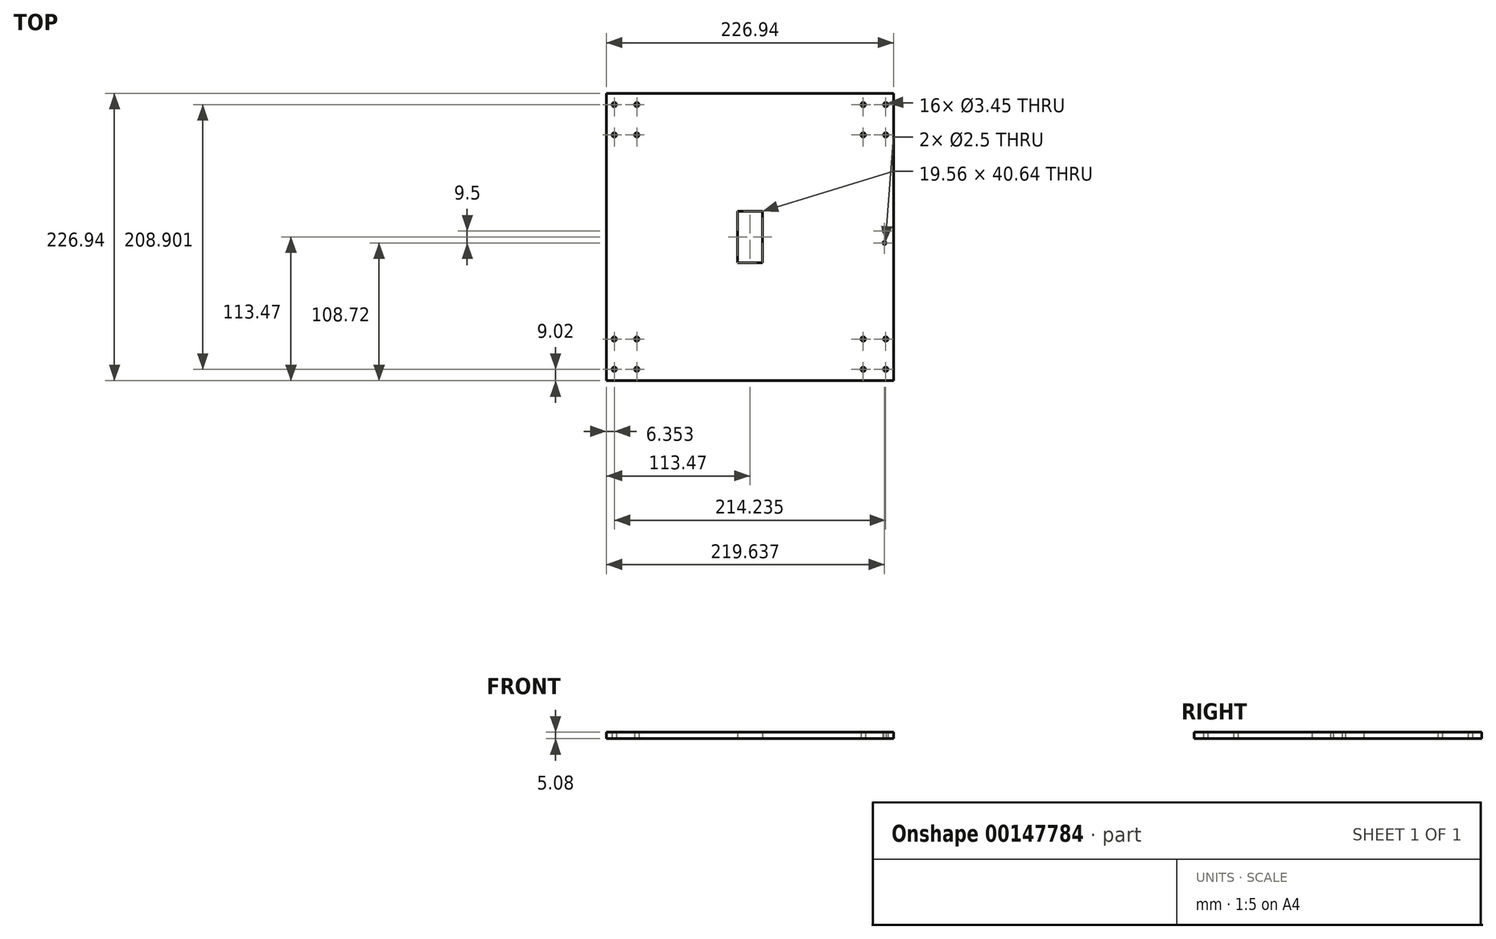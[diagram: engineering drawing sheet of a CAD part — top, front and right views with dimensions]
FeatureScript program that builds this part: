
annotation { "Feature Type Name" : "Feature", "Feature Type Description" : "" }
export const myFeature = defineFeature(function(context is Context, id is Id, definition is map)
    precondition{}
    {
        {
            var Q0;
            Q0=qCreatedBy(makeId("Top.planeOp"),FACE);
            var sketch = newSketch(context, id + "F0", { "sketchPlane" : qUnion([Q0])});
            skLineSegment(sketch, "E0.bottom", {"start": v(113.47, -113.47) * mm, "end": v(-113.47, -113.47) * mm});
            skLineSegment(sketch, "E0.top", {"start": v(113.47, 113.47) * mm, "end": v(-113.47, 113.47) * mm});
            skLineSegment(sketch, "E0.left", {"start": v(113.47, -113.47) * mm, "end": v(113.47, 113.47) * mm});
            skLineSegment(sketch, "E0.right", {"start": v(-113.47, -113.47) * mm, "end": v(-113.47, 113.47) * mm});
            skPoint(sketch, "E0.middle", {"position": v(0, 0) * mm});
            skLineSegment(sketch, "E1", {"start": v(-107.12, 113.47) * mm, "end": v(-107.12, 104.45) * mm, "construction": true});
            skLineSegment(sketch, "E2", {"start": v(-107.12, 104.45) * mm, "end": v(-113.47, 104.45) * mm, "construction": true});
            skLineSegment(sketch, "E3.bottom", {"start": v(-98.23, 92.51) * mm, "end": v(98.23, 92.51) * mm, "construction": true});
            skLineSegment(sketch, "E3.top", {"start": v(-98.23, -92.51) * mm, "end": v(98.23, -92.51) * mm, "construction": true});
            skLineSegment(sketch, "E3.left", {"start": v(-98.23, 92.51) * mm, "end": v(-98.23, -92.51) * mm, "construction": true});
            skLineSegment(sketch, "E3.right", {"start": v(98.23, 92.51) * mm, "end": v(98.23, -92.51) * mm, "construction": true});
            skLineSegment(sketch, "E4.bottom", {"start": v(-107.12, 104.45) * mm, "end": v(-89.34, 104.45) * mm, "construction": true});
            skLineSegment(sketch, "E4.top", {"start": v(-107.12, 80.57) * mm, "end": v(-89.34, 80.57) * mm, "construction": true});
            skLineSegment(sketch, "E4.left", {"start": v(-107.12, 104.45) * mm, "end": v(-107.12, 80.57) * mm, "construction": true});
            skLineSegment(sketch, "E4.right", {"start": v(-89.34, 104.45) * mm, "end": v(-89.34, 80.57) * mm, "construction": true});
            skPoint(sketch, "E4.middle", {"position": v(-98.23, 92.51) * mm});
            skLineSegment(sketch, "E5.bottom", {"start": v(107.12, 104.45) * mm, "end": v(89.34, 104.45) * mm, "construction": true});
            skLineSegment(sketch, "E5.top", {"start": v(107.12, 80.57) * mm, "end": v(89.34, 80.57) * mm, "construction": true});
            skLineSegment(sketch, "E5.left", {"start": v(107.12, 104.45) * mm, "end": v(107.12, 80.57) * mm, "construction": true});
            skLineSegment(sketch, "E5.right", {"start": v(89.34, 104.45) * mm, "end": v(89.34, 80.57) * mm, "construction": true});
            skPoint(sketch, "E5.middle", {"position": v(98.23, 92.51) * mm});
            skLineSegment(sketch, "E6.bottom", {"start": v(107.12, -104.45) * mm, "end": v(89.34, -104.45) * mm, "construction": true});
            skLineSegment(sketch, "E6.top", {"start": v(107.12, -80.57) * mm, "end": v(89.34, -80.57) * mm, "construction": true});
            skLineSegment(sketch, "E6.left", {"start": v(107.12, -104.45) * mm, "end": v(107.12, -80.57) * mm, "construction": true});
            skLineSegment(sketch, "E6.right", {"start": v(89.34, -104.45) * mm, "end": v(89.34, -80.57) * mm, "construction": true});
            skPoint(sketch, "E6.middle", {"position": v(98.23, -92.51) * mm});
            skLineSegment(sketch, "E7.bottom", {"start": v(-89.34, -104.45) * mm, "end": v(-107.12, -104.45) * mm, "construction": true});
            skLineSegment(sketch, "E7.top", {"start": v(-89.34, -80.57) * mm, "end": v(-107.12, -80.57) * mm, "construction": true});
            skLineSegment(sketch, "E7.left", {"start": v(-89.34, -104.45) * mm, "end": v(-89.34, -80.57) * mm, "construction": true});
            skLineSegment(sketch, "E7.right", {"start": v(-107.12, -104.45) * mm, "end": v(-107.12, -80.57) * mm, "construction": true});
            skPoint(sketch, "E7.middle", {"position": v(-98.23, -92.51) * mm});
            skCircle(sketch, "E8", {"center": v(-107.12, 104.45) * mm, "radius": 1.73 * mm});
            skCircle(sketch, "E9", {"center": v(-89.34, 104.45) * mm, "radius": 1.73 * mm});
            skCircle(sketch, "E10", {"center": v(-89.34, 80.57) * mm, "radius": 1.73 * mm});
            skCircle(sketch, "E11", {"center": v(-107.12, 80.57) * mm, "radius": 1.73 * mm});
            skCircle(sketch, "E12", {"center": v(107.12, 80.57) * mm, "radius": 1.73 * mm});
            skCircle(sketch, "E13", {"center": v(107.12, 104.45) * mm, "radius": 1.73 * mm});
            skCircle(sketch, "E14", {"center": v(89.34, 104.45) * mm, "radius": 1.73 * mm});
            skCircle(sketch, "E15", {"center": v(89.34, 80.57) * mm, "radius": 1.73 * mm});
            skCircle(sketch, "E16", {"center": v(107.12, -104.45) * mm, "radius": 1.73 * mm});
            skCircle(sketch, "E17", {"center": v(107.12, -80.57) * mm, "radius": 1.73 * mm});
            skCircle(sketch, "E18", {"center": v(89.34, -80.57) * mm, "radius": 1.73 * mm});
            skCircle(sketch, "E19", {"center": v(89.34, -104.45) * mm, "radius": 1.73 * mm});
            skCircle(sketch, "E20", {"center": v(-89.34, -104.45) * mm, "radius": 1.73 * mm});
            skCircle(sketch, "E21", {"center": v(-89.34, -80.57) * mm, "radius": 1.73 * mm});
            skCircle(sketch, "E22", {"center": v(-107.12, -80.57) * mm, "radius": 1.73 * mm});
            skCircle(sketch, "E23", {"center": v(-107.12, -104.45) * mm, "radius": 1.73 * mm});
            skLineSegment(sketch, "E24.bottom", {"start": v(9.78, 20.32) * mm, "end": v(-9.78, 20.32) * mm});
            skLineSegment(sketch, "E24.top", {"start": v(9.78, -20.32) * mm, "end": v(-9.78, -20.32) * mm});
            skLineSegment(sketch, "E24.left", {"start": v(9.78, 20.32) * mm, "end": v(9.78, -20.32) * mm});
            skLineSegment(sketch, "E24.right", {"start": v(-9.78, 20.32) * mm, "end": v(-9.78, -20.32) * mm});
            skLineSegment(sketch, "E25", {"start": v(113.47, 0) * mm, "end": v(106.17, 0) * mm, "construction": true});
            skLineSegment(sketch, "E26", {"start": v(106.17, 4.75) * mm, "end": v(106.17, -4.75) * mm, "construction": true});
            skCircle(sketch, "E27", {"center": v(106.17, 4.75) * mm, "radius": 1.25 * mm});
            skCircle(sketch, "E28", {"center": v(106.17, -4.75) * mm, "radius": 1.25 * mm});
            skSolve(sketch);
        }
        {
            var Q0;
            Q0=qSketchRegion(id+"F0",true);
            extrude(context, id + "F1", {"entities" : qUnion([Q0]), "depth" : 5.08 * mm});
        }
    });
